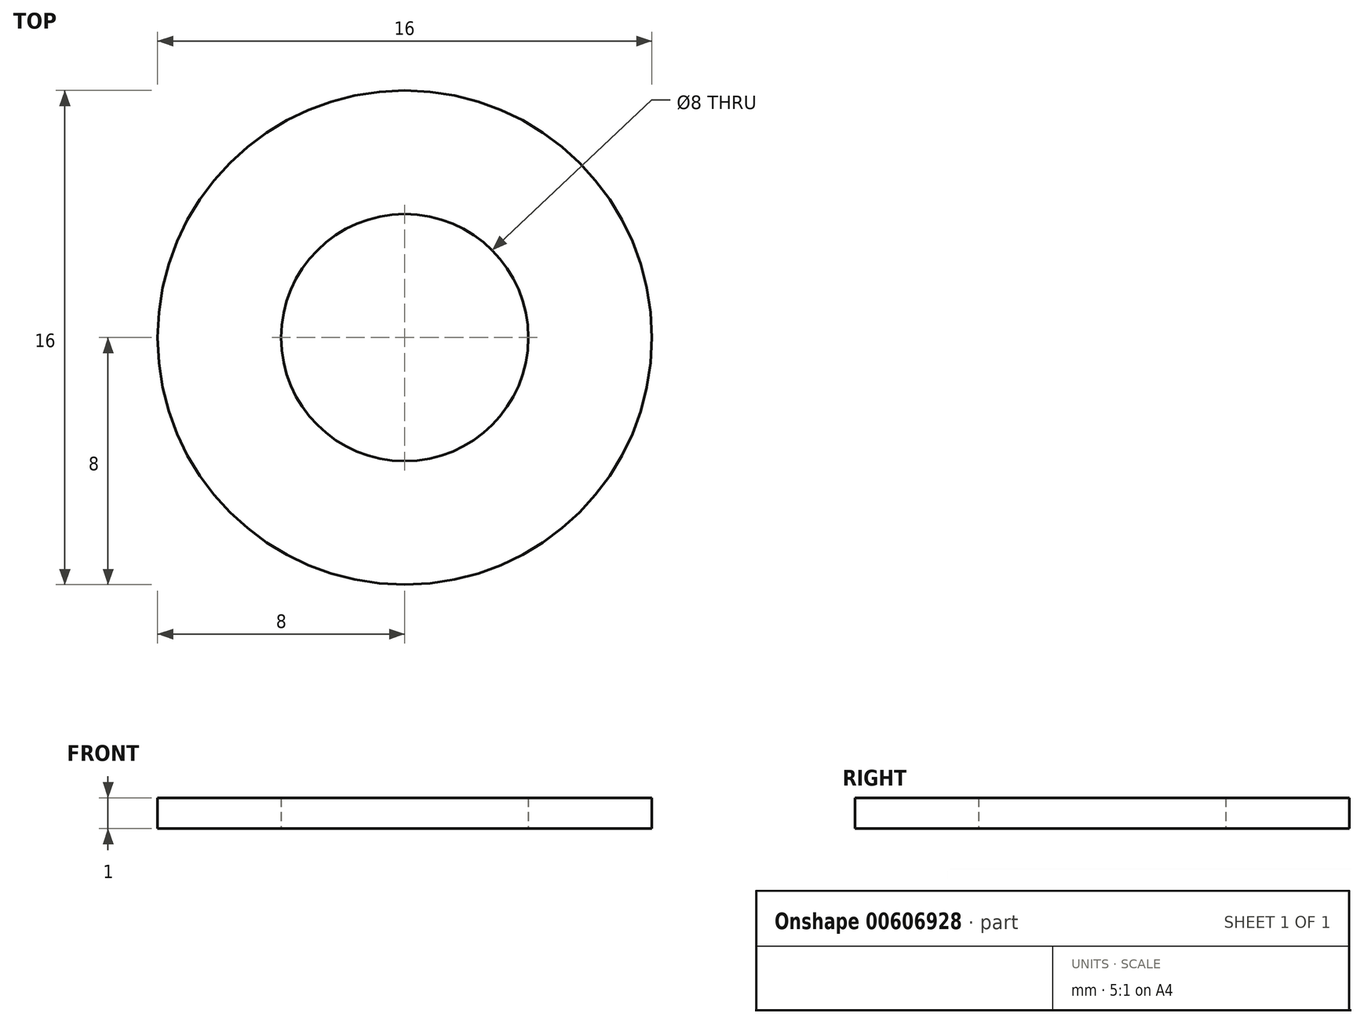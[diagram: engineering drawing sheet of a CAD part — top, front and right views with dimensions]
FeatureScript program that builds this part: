
annotation { "Feature Type Name" : "Feature", "Feature Type Description" : "" }
export const myFeature = defineFeature(function(context is Context, id is Id, definition is map)
    precondition{}
    {
        {
            var Q0;
            Q0=qCreatedBy(makeId("Top.planeOp"),FACE);
            var sketch = newSketch(context, id + "F0", { "sketchPlane" : qUnion([Q0]) });
            skCircle(sketch, "E0.0.0", {"center": v(0, 0) * mm, "radius": 8 * mm});
            skCircle(sketch, "E1.0", {"center": v(0, 0) * mm, "radius": 4 * mm});
            skSolve(sketch);
        }
        {
            var Q0;
            Q0=makeQuery(id+"F0.imprint","IMPRINT",FACE,{"disambiguationData":[TD([[makeQuery(id+"F0.imprint","IMPRINT",EDGE,{"derivedFrom":sQuery(id+"F0.wireOp",EDGE,"E0.0.0")}),1.0]])]});
            extrude(context, id + "F1", {"entities" : qUnion([Q0]), "depth" : 1 * mm, "offsetDistance" : 25 * mm});
        }
    });
